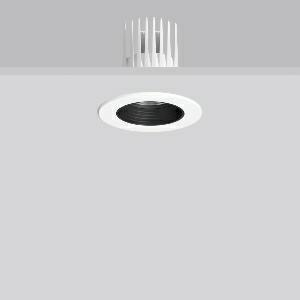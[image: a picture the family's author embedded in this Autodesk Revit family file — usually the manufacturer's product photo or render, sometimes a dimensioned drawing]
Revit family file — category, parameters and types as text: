
# Revit family: heledon_mini_e_901744_002_2_76_b039
name_source: partatom
category: Lighting Fixtures
units: mm (PartAtom-declared; Revit-internal decimal feet)

## family parameters
Cut with Voids When Loaded = No
Host = Face
Light Source = No
Part Type = Normal
Room Calculation Point = No
Round Connector Dimension = Use Diameter
Shared = No

## types (1)
- HELEDON mini E (1 x LED Modul 927, 2000 lm, 2700)
    Apparent Load = 20 VA
    Approval mark = CE
    CIE Flux Codes = 96 100 100 100 100
    Color Rendering = 92
    Color Temperature = 2700
    Default Elevation = 1800 mm
    Description = Series: HELEDON mini
Round recessed downlight. Housing: die-cast aluminium, powder-coated. Black plastic ring and recessed LED to prevent glare from the side. Optical assembly with lens made of plastic (polycarbonate) for the best homogeneous light distribution - can be changed without tools. Best colour rendering index Ra>90. Suitable for Recessed ceiling mounting. Installation without tools thanks to spring fastening system. Including separate LED converter with connecting cable 600 mm.High quality converter without flickering and stroboscopic effect. Through-wiring box (5 pole) available as accessory. The following accessories can be mounted without use of tools: interchangeable lenses, decorative glasses, honeycomb louvre, clear and frosted diffusers, white interchangeable plastic ring. 
Colour: traffic white, matt (RAL 9016)
Diameter: 124 mm
Height: 3 mm
Cut-out diameter: 114 mm
Recess height: 170 mm
Luminaire: recess height: 120 mm
Lamp: LED
Socket: without socket
Colour temperature: 2700K
Colour rendering index (CRI): 92
System power: 20 W
Rated luminous flux: 2000 lm
Luminous efficiency: 100 lm/W
Control gear: Converter, dimmable, DALI
Protection class: II
Type of protection: IP 20
    Height = 0 mm  [stored 0 ft]
    Lamp = 1 x LED Modul 927
    Lamp Light Flux = 2000 lm
    Lamp count = 1
    Length = 124 mm  [stored 0.406824 ft]
    Lifetime = 50000 h
    Luminous efficacy = 100 lm/W
    Manufacturer = RZB
    ModVariant = No
    Model = 901744.002.2.76
    Mounting Place = Ceiling
    Mounting Type = Recessed
    Number of Poles = 1
    OnlyDefault = Yes
    Power Factor = 1
    Product Name = HELEDON mini E
    Product group = Recessed downlights
    ProductGroupID = 402
    Protection Class = Protection class II
    Protection Degree = IP 20
    RLX_Detail_Level = 1
    RLX_Emergency_Light_Flux = 0 lm
    RLX_Emergency_Type = 0
    RLX_Emergency_Type_DB = No
    RlxData = <blob elided: 123865 chars, md5=df3beb7b>
    Socket = socket
    Standby Power = 0 W
    System Light Flux = 2000 lm
    System Power = 20 W
    Type Comments = Product without accessories
    Type Image = 901656.002.jpg
    URL = http://relux.com
    VarID = ---
    Voltage = 230 V
    Voltage Range = 220-240 V
    Weight = 0.00 kg
    Width = 0 mm  [stored 0 ft]

note: [stored X ft] marks values corroborated as IEEE doubles in the binary element streams (Revit-internal decimal feet)

## geometry (parser evidence)
native form markers: Blend x4, Sweep x10
no freeform markers — native parametric forms only
